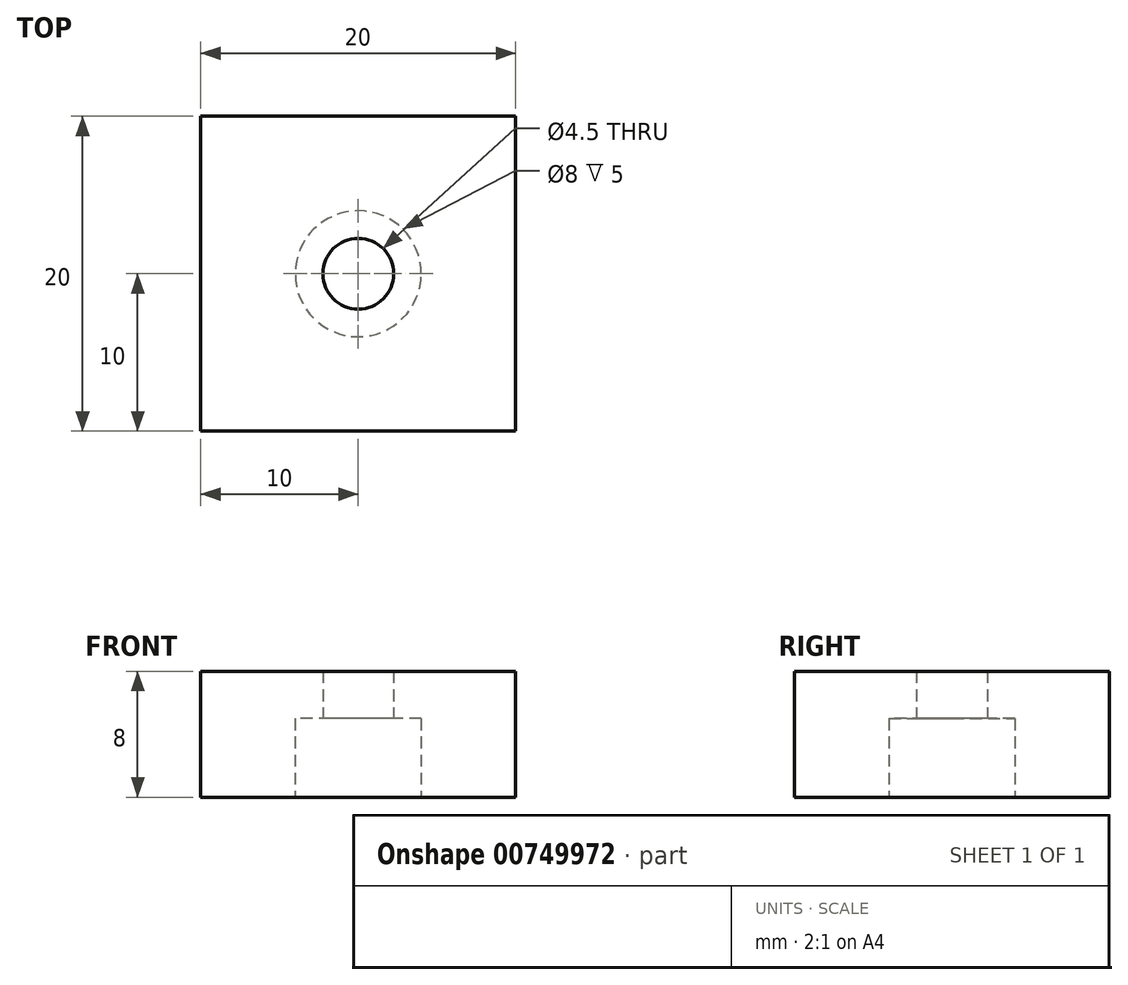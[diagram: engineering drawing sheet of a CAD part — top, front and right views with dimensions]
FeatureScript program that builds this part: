
annotation { "Feature Type Name" : "Feature", "Feature Type Description" : "" }
export const myFeature = defineFeature(function(context is Context, id is Id, definition is map)
    precondition{}
    {
        {
            var Q0;
            Q0=qCreatedBy(makeId("Top.planeOp"),FACE);
            var sketch = newSketch(context, id + "F0", { "sketchPlane" : qUnion([Q0])});
            skLineSegment(sketch, "E0.bottom", {"start": v(10, -10) * mm, "end": v(-10, -10) * mm});
            skLineSegment(sketch, "E0.top", {"start": v(10, 10) * mm, "end": v(-10, 10) * mm});
            skLineSegment(sketch, "E0.left", {"start": v(10, -10) * mm, "end": v(10, 10) * mm});
            skLineSegment(sketch, "E0.right", {"start": v(-10, -10) * mm, "end": v(-10, 10) * mm});
            skPoint(sketch, "E0.middle", {"position": v(0, 0) * mm});
            skCircle(sketch, "E1", {"center": v(0, 0) * mm, "radius": 2.25 * mm});
            skCircle(sketch, "E2", {"center": v(0, 0) * mm, "radius": 4 * mm});
            skSolve(sketch);
        }
        {
            var Q0;
            Q0=makeQuery(id+"F0.imprint","IMPRINT",FACE,{"disambiguationData":[TD([[makeQuery(id+"F0.imprint","IMPRINT",EDGE,{"derivedFrom":sQuery(id+"F0.wireOp",EDGE,"E0.bottom")}),-1.0]])]});
            var Q1;
            Q1=makeQuery(id+"F0.imprint","IMPRINT",FACE,{"disambiguationData":[TD([[makeQuery(id+"F0.imprint","IMPRINT",EDGE,{"derivedFrom":sQuery(id+"F0.wireOp",EDGE,"E1")}),-1.0]])]});
            extrude(context, id + "F1", {"entities" : qUnion([Q0, Q1]), "depth" : 8 * mm, "offsetDistance" : 25 * mm});
        }
        {
            var Q0;
            Q0=makeQuery(id+"F0.imprint","IMPRINT",FACE,{"disambiguationData":[TD([[makeQuery(id+"F0.imprint","IMPRINT",EDGE,{"derivedFrom":sQuery(id+"F0.wireOp",EDGE,"E1")}),-1.0]])]});
            extrude(context, id + "F2", {"entities" : qUnion([Q0]), "operationType" : NewBodyOperationType.REMOVE, "depth" : 5 * mm, "offsetDistance" : 25 * mm});
        }
    });
